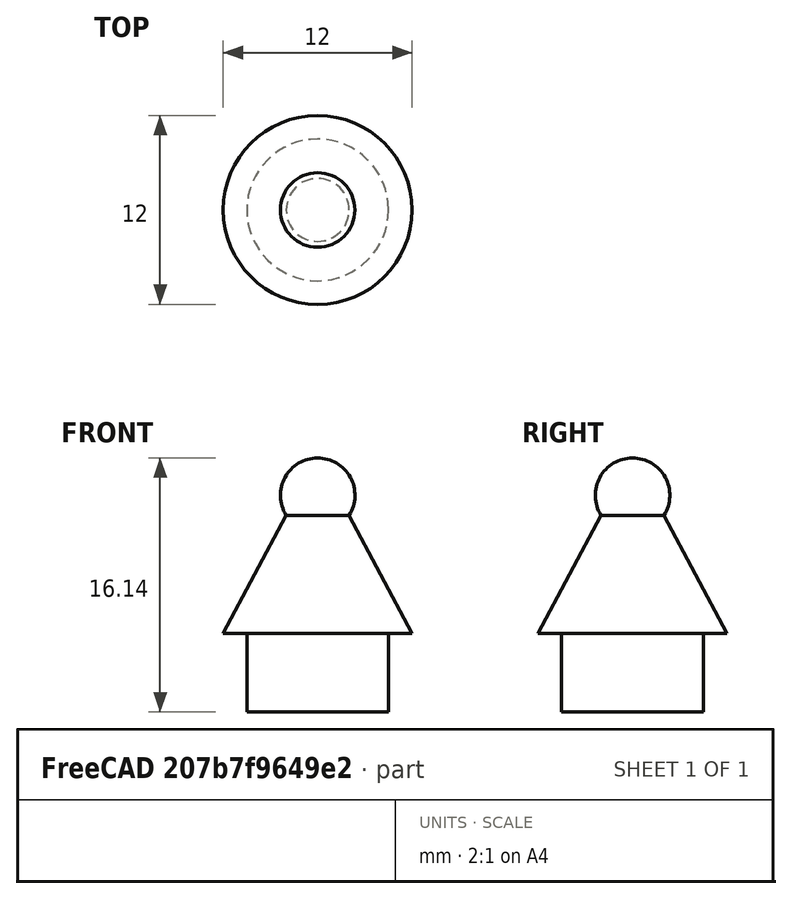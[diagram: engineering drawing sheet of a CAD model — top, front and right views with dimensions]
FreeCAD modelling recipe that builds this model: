
FCSTD DOCUMENT  (FreeCAD 0.19R24276 (Git))
Label: peaoLudo
License: All rights reserved
LicenseURL: http://en.wikipedia.org/wiki/All_rights_reserved
objects: Sketcher::SketchObject×1, PartDesign::Revolution×1, PartDesign::Body×1
note: 4 computed .brp shape members not serialized (recipe doc carries the construction recipe); baked Part::Feature solids carry a one-line shape summary decoded from their .brp

FEATURE [Sketcher::SketchObject] Sketch
  FullyConstrained = false
  MapMode = 5
  Placement = pos=(0,0,0) rot=(1,0,0;1.5708rad)
  Support = -> [XZ_Plane]
  sketch-geometry (6):
    g0: LineSegment StartX=4.5 StartY=0 StartZ=0 EndX=4.5 EndY=-5 EndZ=0
    g1: LineSegment StartX=4.5 StartY=-5 StartZ=0 EndX=0 EndY=-5 EndZ=0
    g2: LineSegment StartX=4.5 StartY=0 StartZ=0 EndX=6 EndY=0 EndZ=0
    g3: LineSegment StartX=6 StartY=0 StartZ=0 EndX=2 EndY=7.5 EndZ=0
    g4: ArcOfCircle CenterX=0 CenterY=8.76735 CenterZ=0 NormalX=0 NormalY=0 NormalZ=1 AngleXU=0 Radius=2.36774 StartAngle=5.71837 EndAngle=7.85398
    g5: LineSegment StartX=7e-16 StartY=11.1351 StartZ=0 EndX=0 EndY=-5 EndZ=0
  constraints (18):
    c: PointOnObject(g0,g-1)
    c: Vertical(g0)
    c: DistanceY(g0,g0) = 5
    c: DistanceX(g-1,g0) = 4.5
    c: Coincident(g1,g0)
    c: Horizontal(g1)
    c: DistanceX(g1,g1) = 4.5
    c: Coincident(g2,g0)
    c: Horizontal(g2)
    c: DistanceX(g2,g2) = 1.5
    c: Coincident(g3,g2)
    c: DistanceX(g-1,g3) = 2
    c: DistanceY(g3) = 7.5
    c: Coincident(g3,g4)
    c: DistanceX(g-1,g4) = 0
    c: DistanceX(g-1,g4) = 0
    c: Coincident(g5,g4)
    c: Coincident(g5,g1)
FEATURE [PartDesign::Revolution] Revolution
  Angle = 360
  Axis = (0,2e-16,1)
  Base = (0,0,0)
  Placement = pos=(0,0,0) rot=(1,0,0;1.5708rad)
  Profile = -> Sketch
  ReferenceAxis = -> Sketch [V_Axis]
  Reversed = true
FEATURE [PartDesign::Body] Body
  Group = -> [Sketch,Revolution]
  Origin = -> Origin
  Tip = -> Revolution
